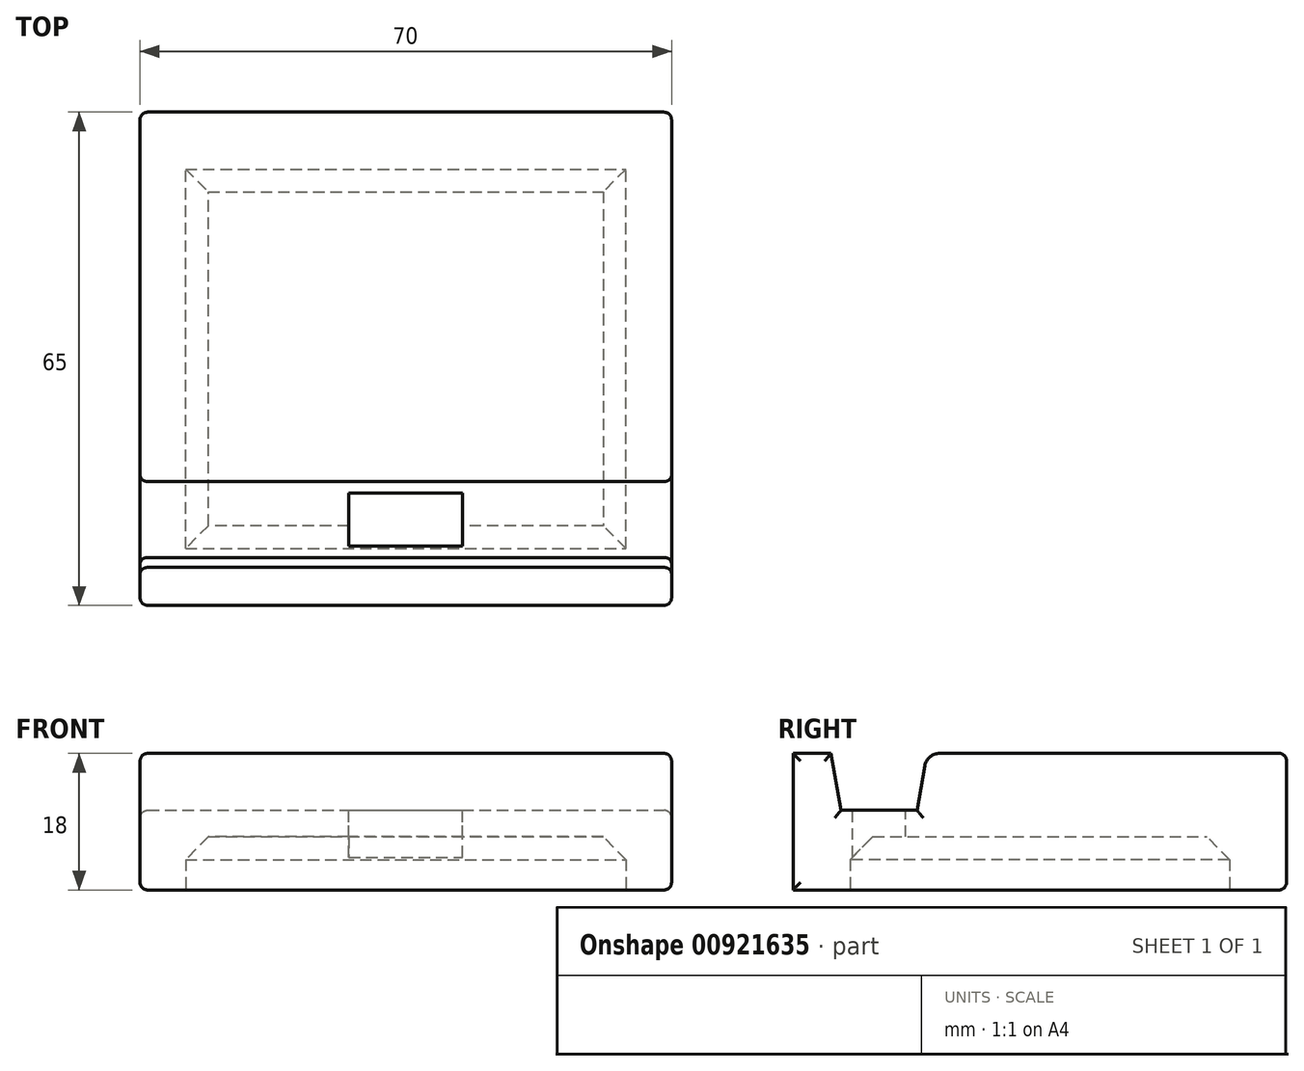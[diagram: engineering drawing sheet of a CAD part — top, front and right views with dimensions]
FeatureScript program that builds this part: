
annotation { "Feature Type Name" : "Feature", "Feature Type Description" : "" }
export const myFeature = defineFeature(function(context is Context, id is Id, definition is map)
    precondition{}
    {
        {
            var Q0;
            Q0=qCreatedBy(makeId("Right.planeOp"),FACE);
            var sketch = newSketch(context, id + "F0", { "sketchPlane" : qUnion([Q0])});
            skLineSegment(sketch, "E0.bottom", {"start": v(-32.5, 9) * mm, "end": v(32.5, 9) * mm});
            skLineSegment(sketch, "E0.top", {"start": v(-32.5, -9) * mm, "end": v(32.5, -9) * mm});
            skLineSegment(sketch, "E0.left", {"start": v(-32.5, 9) * mm, "end": v(-32.5, -9) * mm});
            skLineSegment(sketch, "E0.right", {"start": v(32.5, 9) * mm, "end": v(32.5, -9) * mm});
            skPoint(sketch, "E0.middle", {"position": v(0, 0) * mm});
            skSolve(sketch);
        }
        {
            var Q0;
            Q0=makeQuery(id+"F0.imprint","IMPRINT",FACE,{"disambiguationData":[TD([[makeQuery(id+"F0.imprint","IMPRINT",EDGE,{"derivedFrom":sQuery(id+"F0.wireOp",EDGE,"E0.bottom")}),-1.0]])]});
            extrude(context, id + "F1", {"entities" : qUnion([Q0]), "endBound" : BoundingType.SYMMETRIC, "depth" : 70 * mm, "offsetDistance" : 25 * mm});
        }
        {
            var Q0;
            Q0=makeQuery(id+"F1.opExtrude","CAP_FACE",FACE,{"disambiguationData":[OSD([sQuery(id+"F0.wireOp",EDGE,"E0.bottom"),sQuery(id+"F0.wireOp",EDGE,"E0.top"),sQuery(id+"F0.wireOp",EDGE,"E0.left"),sQuery(id+"F0.wireOp",EDGE,"E0.right")])],"isStart":false});
            var sketch = newSketch(context, id + "F2", { "sketchPlane" : qUnion([Q0])});
            skLineSegment(sketch, "E1", {"start": v(-32.5, 9) * mm, "end": v(-27.5, 9) * mm});
            skLineSegment(sketch, "E2", {"start": v(-27.5, 9) * mm, "end": v(-26.18, 1.5) * mm});
            skLineSegment(sketch, "E3", {"start": v(-26.18, 1.5) * mm, "end": v(-16.18, 1.5) * mm});
            skLineSegment(sketch, "E4", {"start": v(-16.18, 1.5) * mm, "end": v(-14.86, 9) * mm});
            skLineSegment(sketch, "E5", {"start": v(-32.5, 9) * mm, "end": v(-21.55, 13.53) * mm});
            skLineSegment(sketch, "E6", {"start": v(-21.55, 13.53) * mm, "end": v(-14.86, 9) * mm});
            skSolve(sketch);
        }
        {
            var Q0;
            {var subQ0=sQuery(id+"F2.wireOp",EDGE,"E2");Q0=makeQuery(id+"F2.imprint","IMPRINT",FACE,{"disambiguationData":[TD([[makeQuery(id+"F2.imprint","IMPRINT",EDGE,{"derivedFrom":subQ0}),1.0]])]});}
            var Q1;
            {var subQ0=sQuery(id+"F2.wireOp",EDGE,"E1");Q1=makeQuery(id+"F2.imprint","IMPRINT",FACE,{"disambiguationData":[TD([[makeQuery(id+"F2.imprint","IMPRINT",EDGE,{"derivedFrom":subQ0}),1.0]])]});}
            extrude(context, id + "F3", {"entities" : qUnion([Q0, Q1]), "operationType" : NewBodyOperationType.REMOVE, "endBound" : BoundingType.THROUGH_ALL, "oppositeDirection" : true, "depth" : 25 * mm, "offsetDistance" : 25 * mm});
        }
        {
            var Q0;
            Q0=makeQuery(id+"F3.boolean.opBoolean","COPY",EDGE,{"derivedFrom":makeQuery(id+"F3.opExtrude","SWEPT_EDGE",EDGE,{"disambiguationData":[OSD([sQuery(id+"F0.wireOp",EDGE,"E0.bottom"),sQuery(id+"F2.wireOp",EDGE,"E4"),sQuery(id+"F2.wireOp",EDGE,"E6")])]})});
            var Q1;
            Q1=makeQuery(id+"F3.boolean.opBoolean","COPY",EDGE,{"derivedFrom":makeQuery(id+"F3.opExtrude","SWEPT_EDGE",EDGE,{"disambiguationData":[OSD([sQuery(id+"F0.wireOp",EDGE,"E0.bottom"),sQuery(id+"F2.wireOp",EDGE,"E1"),sQuery(id+"F2.wireOp",EDGE,"E2")])]})});
            fillet(context, id + "F4", {"entities" : qUnion([Q0, Q1]), "radius" : 2 * mm, "tangentPropagation" : true, "allowEdgeOverflow" : false});
        }
        {
            var Q0;
            {var subQ0=sQuery(id+"F0.wireOp",EDGE,"E0.bottom");var subQ1=sQuery(id+"F0.wireOp",EDGE,"E0.right");Q0=makeQuery(id+"F3.boolean.opBoolean","SPLIT",EDGE,{"disambiguationData":[TD([makeQuery(id+"F1.opExtrude","SWEPT_FACE",FACE,{"disambiguationData":[OSD([subQ1])]})])],"derivedFrom":makeQuery(id+"F1.opExtrude","CAP_EDGE",EDGE,{"disambiguationData":[OSD([subQ0])],"isStart":false})});}
            var Q1;
            Q1=makeQuery(id+"F1.opExtrude","CAP_FACE",FACE,{"disambiguationData":[OSD([sQuery(id+"F0.wireOp",EDGE,"E0.bottom"),sQuery(id+"F0.wireOp",EDGE,"E0.top"),sQuery(id+"F0.wireOp",EDGE,"E0.left"),sQuery(id+"F0.wireOp",EDGE,"E0.right")])],"isStart":false});
            var Q2;
            Q2=makeQuery(id+"F1.opExtrude","SWEPT_FACE",FACE,{"disambiguationData":[OSD([sQuery(id+"F0.wireOp",EDGE,"E0.right")])]});
            var Q3;
            Q3=makeQuery(id+"F1.opExtrude","CAP_FACE",FACE,{"disambiguationData":[OSD([sQuery(id+"F0.wireOp",EDGE,"E0.bottom"),sQuery(id+"F0.wireOp",EDGE,"E0.top"),sQuery(id+"F0.wireOp",EDGE,"E0.left"),sQuery(id+"F0.wireOp",EDGE,"E0.right")])],"isStart":true});
            fillet(context, id + "F5", {"entities" : qUnion([Q0, Q1, Q2, Q3]), "radius" : 1 * mm, "tangentPropagation" : true, "allowEdgeOverflow" : false});
        }
        {
            var Q0;
            Q0=qCreatedBy(makeId("Right.planeOp"),FACE);
            var sketch = newSketch(context, id + "F6", { "sketchPlane" : qUnion([Q0])});
            skLineSegment(sketch, "E7.0", {"start": v(-15.34, 0.5) * mm, "end": v(-27.02, 0.5) * mm});
            skLineSegment(sketch, "E8.bottom", {"start": v(-17.68, -2.5) * mm, "end": v(-24.68, -2.5) * mm});
            skLineSegment(sketch, "E8.top", {"start": v(-17.68, 3.5) * mm, "end": v(-24.68, 3.5) * mm});
            skLineSegment(sketch, "E8.left", {"start": v(-17.68, -2.5) * mm, "end": v(-17.68, 3.5) * mm});
            skLineSegment(sketch, "E8.right", {"start": v(-24.68, -2.5) * mm, "end": v(-24.68, 3.5) * mm});
            skPoint(sketch, "E8.middle", {"position": v(-21.18, 0.5) * mm});
            skSolve(sketch);
        }
        {
            var Q0;
            Q0 = qSketchRegion(id + "F6", true);
            extrude(context, id + "F7", {"entities" : qUnion([Q0]), "operationType" : NewBodyOperationType.REMOVE, "endBound" : BoundingType.SYMMETRIC, "oppositeDirection" : true, "depth" : 15 * mm, "offsetDistance" : 25 * mm});
        }
        {
            var Q0;
            Q0=makeQuery(id+"F1.opExtrude","SWEPT_FACE",FACE,{"disambiguationData":[OSD([sQuery(id+"F0.wireOp",EDGE,"E0.top")])]});
            var sketch = newSketch(context, id + "F8", { "sketchPlane" : qUnion([Q0])});
            skLineSegment(sketch, "E9.bottom", {"start": v(-29, 25) * mm, "end": v(29, 25) * mm});
            skLineSegment(sketch, "E9.top", {"start": v(-29, -25) * mm, "end": v(29, -25) * mm});
            skLineSegment(sketch, "E9.left", {"start": v(-29, 25) * mm, "end": v(-29, -25) * mm});
            skLineSegment(sketch, "E9.right", {"start": v(29, 25) * mm, "end": v(29, -25) * mm});
            skPoint(sketch, "E9.middle", {"position": v(0, 0) * mm});
            skSolve(sketch);
        }
        {
            var Q0;
            Q0=makeQuery(id+"F8.imprint","IMPRINT",FACE,{"disambiguationData":[TD([[makeQuery(id+"F8.imprint","IMPRINT",EDGE,{"derivedFrom":sQuery(id+"F8.wireOp",EDGE,"E9.bottom")}),-1.0]])]});
            var Q1;
            Q1=makeQuery(id+"F1.opExtrude","SWEPT_FACE",FACE,{"disambiguationData":[OSD([sQuery(id+"F0.wireOp",EDGE,"E0.top")])]});
            extrude(context, id + "F9", {"entities" : qUnion([Q0]), "operationType" : NewBodyOperationType.REMOVE, "oppositeDirection" : true, "depth" : 7 * mm, "endBoundEntityFace" : qUnion([Q1]), "offsetDistance" : 25 * mm});
        }
        {
            var Q0;
            Q0=makeQuery(id+"F9.boolean.opBoolean","COPY",EDGE,{"derivedFrom":makeQuery(id+"F9.opExtrude","CAP_EDGE",EDGE,{"disambiguationData":[OSD([sQuery(id+"F8.wireOp",EDGE,"E9.right")])],"isStart":false})});
            var Q1;
            Q1=makeQuery(id+"F9.boolean.opBoolean","COPY",EDGE,{"derivedFrom":makeQuery(id+"F9.opExtrude","CAP_EDGE",EDGE,{"disambiguationData":[OSD([sQuery(id+"F8.wireOp",EDGE,"E9.top")])],"isStart":false})});
            var Q2;
            Q2=makeQuery(id+"F9.boolean.opBoolean","COPY",EDGE,{"derivedFrom":makeQuery(id+"F9.opExtrude","CAP_EDGE",EDGE,{"disambiguationData":[OSD([sQuery(id+"F8.wireOp",EDGE,"E9.left")])],"isStart":false})});
            var Q3;
            Q3=makeQuery(id+"F9.boolean.opBoolean","COPY",EDGE,{"derivedFrom":makeQuery(id+"F9.opExtrude","CAP_EDGE",EDGE,{"disambiguationData":[OSD([sQuery(id+"F8.wireOp",EDGE,"E9.bottom")])],"isStart":false})});
            chamfer(context, id + "F10", {"entities" : qUnion([Q0, Q1, Q2, Q3]), "width" : 3 * mm, "tangentPropagation" : true});
        }
    });
